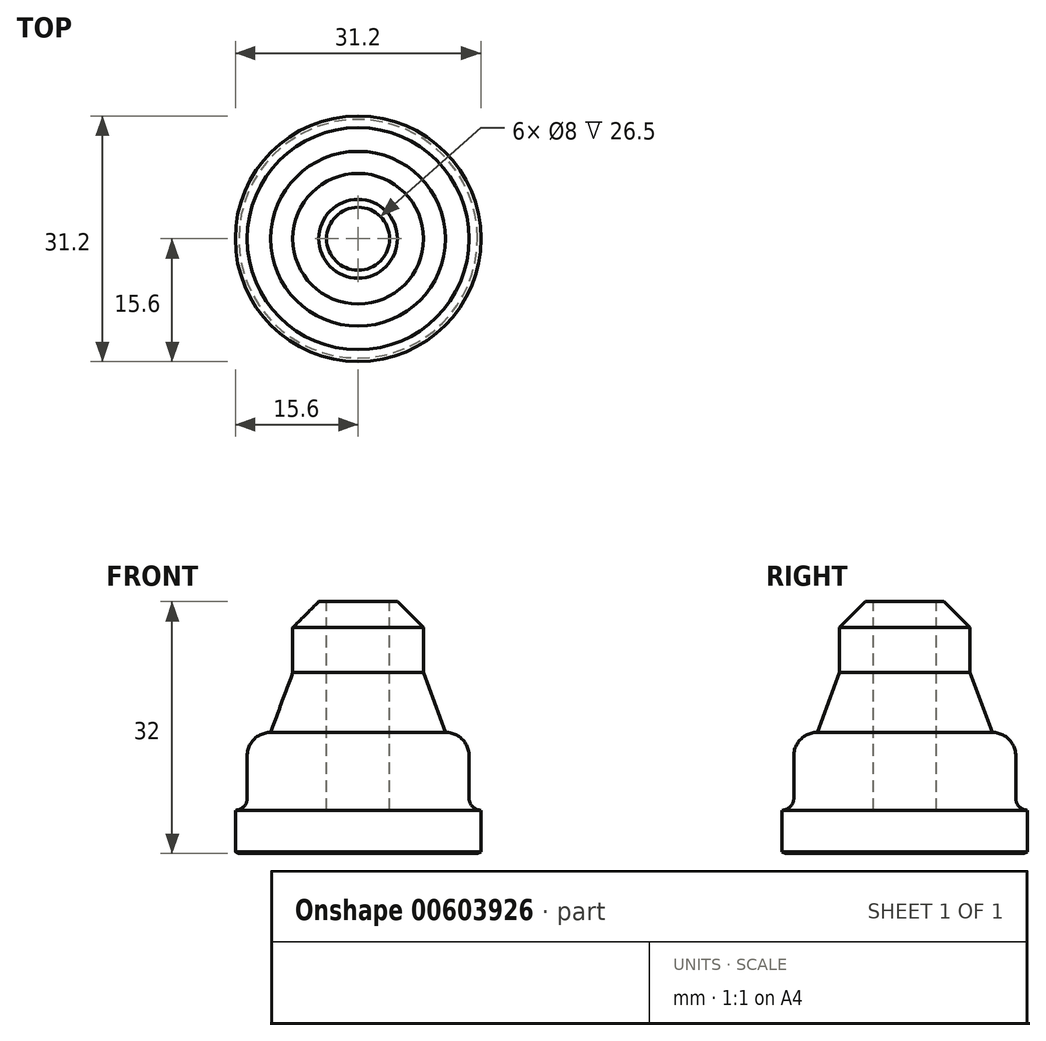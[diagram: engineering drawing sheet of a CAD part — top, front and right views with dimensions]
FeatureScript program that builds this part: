
annotation { "Feature Type Name" : "Feature", "Feature Type Description" : "" }
export const myFeature = defineFeature(function(context is Context, id is Id, definition is map)
    precondition{}
    {
        {
            var Q0;
            Q0=qCreatedBy(makeId("Front.planeOp"),FACE);
            var sketch = newSketch(context, id + "F0", { "sketchPlane" : qUnion([Q0])});
            skLineSegment(sketch, "E0", {"start": v(0, -23) * mm, "end": v(0, 19.2) * mm});
            skLineSegment(sketch, "E1", {"start": v(14.1, -16) * mm, "end": v(14.1, -10.6) * mm});
            skArc(sketch, "E2", {"start": v(14.1, -10.6) * mm, "mid": v(13.22, -8.48) * mm, "end": v(11.1, -7.6) * mm});
            skLineSegment(sketch, "E3", {"start": v(11.1, -7.6) * mm, "end": v(8.3, 0) * mm});
            skLineSegment(sketch, "E4", {"start": v(8.3, 5.7) * mm, "end": v(8.3, 0) * mm});
            skLineSegment(sketch, "E5", {"start": v(8.3, 5.7) * mm, "end": v(5, 9) * mm});
            skLineSegment(sketch, "E6", {"start": v(0, 9) * mm, "end": v(5, 9) * mm});
            skArc(sketch, "E7", {"start": v(14.1, -16) * mm, "mid": v(14.54, -17.06) * mm, "end": v(15.6, -17.5) * mm});
            skArc(sketch, "E8.MirrorCS", {"start": v(-14.1, -16) * mm, "mid": v(-14.54, -17.06) * mm, "end": v(-15.6, -17.5) * mm});
            skLineSegment(sketch, "E9.MirrorCS", {"start": v(-14.1, -16) * mm, "end": v(-14.1, -10.6) * mm});
            skArc(sketch, "E10.MirrorCS", {"start": v(-14.1, -10.6) * mm, "mid": v(-13.22, -8.48) * mm, "end": v(-11.1, -7.6) * mm});
            skLineSegment(sketch, "E11.MirrorCS", {"start": v(-11.1, -7.6) * mm, "end": v(-8.3, 0) * mm});
            skLineSegment(sketch, "E12.MirrorCS", {"start": v(-8.3, 5.7) * mm, "end": v(-8.3, 0) * mm});
            skLineSegment(sketch, "E13.MirrorCS", {"start": v(-8.3, 5.7) * mm, "end": v(-5, 9) * mm});
            skLineSegment(sketch, "E14.MirrorCS", {"start": v(0, 9) * mm, "end": v(-5, 9) * mm});
            skLineSegment(sketch, "E15", {"start": v(15.15, -23) * mm, "end": v(15.6, -22.78) * mm});
            skLineSegment(sketch, "E16", {"start": v(15.6, -22.78) * mm, "end": v(15.6, -17.5) * mm});
            skLineSegment(sketch, "E17", {"start": v(15.15, -23) * mm, "end": v(0, -23) * mm});
            skLineSegment(sketch, "E18.MirrorCS", {"start": v(-15.15, -23) * mm, "end": v(0, -23) * mm});
            skLineSegment(sketch, "E19.MirrorCS", {"start": v(-15.15, -23) * mm, "end": v(-15.6, -22.78) * mm});
            skLineSegment(sketch, "E20", {"start": v(-15.6, -22.78) * mm, "end": v(-15.6, -17.5) * mm});
            skSolve(sketch);
        }
        {
            var Q0;
            Q0=makeQuery(id+"F0.imprint","IMPRINT",FACE,{"disambiguationData":[TD([[makeQuery(id+"F0.imprint","IMPRINT",EDGE,{"derivedFrom":sQuery(id+"F0.wireOp",EDGE,"E1")}),1.0]])]});
            var Q1;
            Q1=sQuery(id+"F0.wireOp",EDGE,"E0");
            revolve(context, id + "F1", {"entities" : qUnion([Q0]), "axis" : qUnion([Q1]), "revolveType" : RevolveType.FULL});
        }
        {
            var Q0;
            Q0=makeQuery(id+"F1.opRevolve","SWEPT_FACE",FACE,{"disambiguationData":[OSD([sQuery(id+"F0.wireOp",EDGE,"E6")])]});
            var sketch = newSketch(context, id + "F2", { "sketchPlane" : qUnion([Q0])});
            skCircle(sketch, "E21", {"center": v(0, 0) * mm, "radius": 4 * mm});
            skSolve(sketch);
        }
        {
            var Q0;
            Q0=makeQuery(id+"F2.imprint","IMPRINT",FACE,{"disambiguationData":[TD([[makeQuery(id+"F2.imprint","IMPRINT",EDGE,{"derivedFrom":sQuery(id+"F2.wireOp",EDGE,"E21")}),1.0]])]});
            extrude(context, id + "F3", {"entities" : qUnion([Q0]), "operationType" : NewBodyOperationType.REMOVE, "oppositeDirection" : true, "depth" : 26.5 * mm, "offsetDistance" : 25 * mm});
        }
    });
